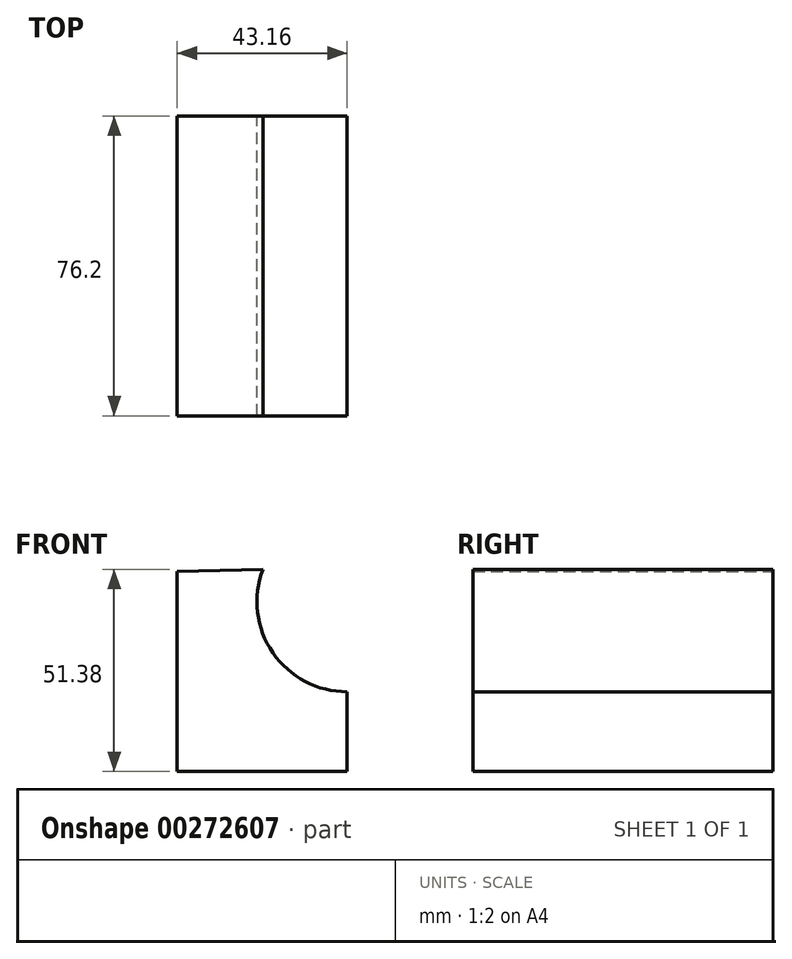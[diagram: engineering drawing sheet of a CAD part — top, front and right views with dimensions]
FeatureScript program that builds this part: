
annotation { "Feature Type Name" : "Feature", "Feature Type Description" : "" }
export const myFeature = defineFeature(function(context is Context, id is Id, definition is map)
    precondition{}
    {
        {
            var Q0;
            Q0=qCreatedBy(makeId("Front.planeOp"),FACE);
            var sketch = newSketch(context, id + "F0", { "sketchPlane" : qUnion([Q0])});
            skLineSegment(sketch, "E0", {"start": v(0, 0) * mm, "end": v(-43.16, 0) * mm});
            skLineSegment(sketch, "E1", {"start": v(-43.16, 0) * mm, "end": v(-43.16, 50.8) * mm});
            skLineSegment(sketch, "E2", {"start": v(0, 0) * mm, "end": v(0, 20.26) * mm});
            skLineSegment(sketch, "E3", {"start": v(-21.36, 51.38) * mm, "end": v(-43.16, 50.8) * mm});
            skArc(sketch, "E4", {"start": v(-21.36, 51.38) * mm, "mid": v(-18.87, 30.2) * mm, "end": v(0, 20.26) * mm});
            skSolve(sketch);
        }
        {
            var Q0;
            Q0 = qSketchRegion(id + "F0", true);
            extrude(context, id + "F1", {"entities" : qUnion([Q0]), "depth" : 76.2 * mm});
        }
    });
